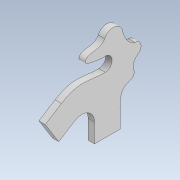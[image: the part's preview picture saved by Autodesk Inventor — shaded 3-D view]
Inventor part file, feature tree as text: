
AUTODESK INVENTOR PART (.ipt)
format: ipt  version: 2021 (Build 250183000, 183)  size: 150,016 bytes
history: native  units: mm
features: other x1, extrude x1, sketch x1
ambient origin geometry x8: Origin, YZ Plane, XZ Plane, XY Plane, X Axis, Y Axis, Z Axis, Center Point
bodies: Body1 (feature_tree)
feature tree (3):
  other  "Sólido1"
  extrude  "Extrusión1"  Depth=5.0mm TaperAngle=0.0deg
  sketch  "Boceto1"  dims[d0=20.0mm d1=60.0deg d2=15.0mm d3=11.0mm d4=15.0mm d5=10.0mm d6=8.0mm d7=0.349066mm d8=50.0mm d9=5.0mm d10=0.0mm]
